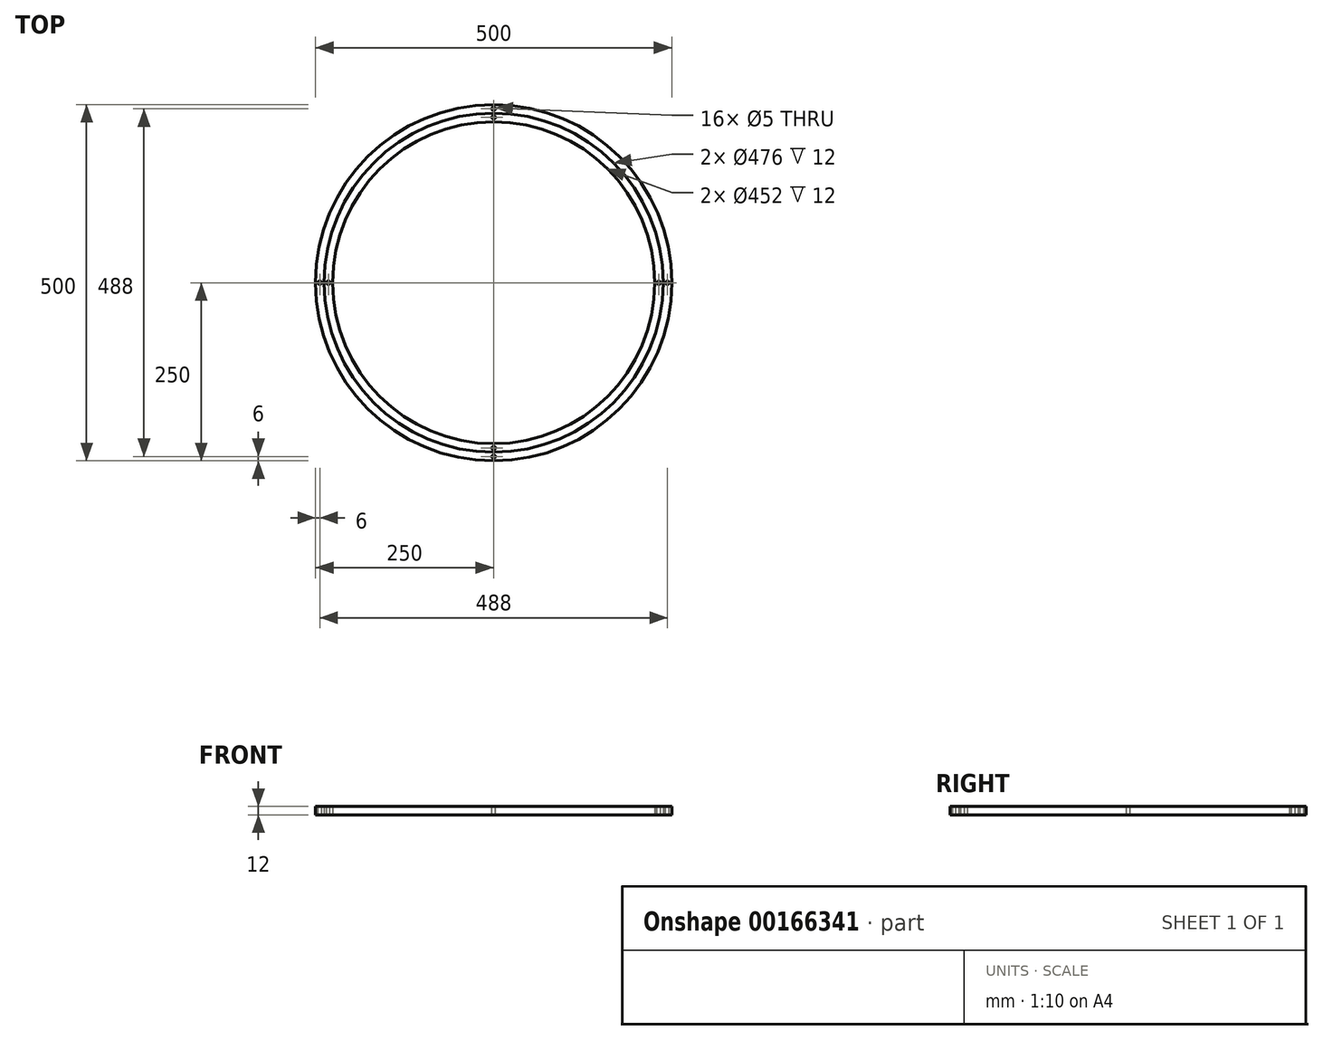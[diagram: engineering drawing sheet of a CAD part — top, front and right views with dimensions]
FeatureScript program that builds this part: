
annotation { "Feature Type Name" : "Feature", "Feature Type Description" : "" }
export const myFeature = defineFeature(function(context is Context, id is Id, definition is map)
    precondition{}
    {
        {
            var Q0;
            Q0=qCreatedBy(makeId("Top.planeOp"),FACE);
            var sketch = newSketch(context, id + "F0", { "sketchPlane" : qUnion([Q0])});
            skCircle(sketch, "E0", {"center": v(0, 0) * mm, "radius": 250 * mm});
            skCircle(sketch, "E1", {"center": v(0, 0) * mm, "radius": 238 * mm});
            skSolve(sketch);
        }
        {
            var Q0;
            Q0=makeQuery(id+"F0.imprint","IMPRINT",FACE,{"disambiguationData":[TD([[makeQuery(id+"F0.imprint","IMPRINT",EDGE,{"derivedFrom":sQuery(id+"F0.wireOp",EDGE,"E0")}),1.0]])]});
            extrude(context, id + "F1", {"entities" : qUnion([Q0]), "depth" : 12 * mm});
        }
        {
            var Q0;
            Q0=qCreatedBy(makeId("Top.planeOp"),FACE);
            var sketch = newSketch(context, id + "F2", { "sketchPlane" : qUnion([Q0])});
            skCircle(sketch, "E2", {"center": v(0, 0) * mm, "radius": 238 * mm});
            skCircle(sketch, "E3", {"center": v(0, 0) * mm, "radius": 226 * mm});
            skSolve(sketch);
        }
        {
            var Q0;
            Q0 = qSketchRegion(id + "F2", true);
            extrude(context, id + "F3", {"entities" : qUnion([Q0]), "depth" : 12 * mm});
        }
        {
            var Q0;
            Q0=makeQuery(id+"F3.opExtrude","CAP_FACE",FACE,{"disambiguationData":[OSD([sQuery(id+"F2.wireOp",EDGE,"E2"),sQuery(id+"F2.wireOp",EDGE,"E3")])],"isStart":false});
            var sketch = newSketch(context, id + "F4", { "sketchPlane" : qUnion([Q0])});
            skLineSegment(sketch, "E4", {"start": v(0, 0) * mm, "end": v(0, 232) * mm});
            skCircle(sketch, "E5", {"center": v(0, 232) * mm, "radius": 2.5 * mm});
            skCircle(sketch, "E6.1.0", {"center": v(-232, 0) * mm, "radius": 2.5 * mm});
            skCircle(sketch, "E6.2.0", {"center": v(0, -232) * mm, "radius": 2.5 * mm});
            skCircle(sketch, "E6.3.0", {"center": v(232, 0) * mm, "radius": 2.5 * mm});
            skPoint(sketch, "E6.center", {"position": v(0, 0) * mm});
            skSolve(sketch);
        }
        {
            var Q0;
            Q0 = qSketchRegion(id + "F4", true);
            extrude(context, id + "F5", {"entities" : qUnion([Q0]), "operationType" : NewBodyOperationType.REMOVE, "oppositeDirection" : true, "depth" : 12 * mm});
        }
        {
            var Q0;
            Q0=makeQuery(id+"F1.opExtrude","CAP_FACE",FACE,{"disambiguationData":[OSD([sQuery(id+"F0.wireOp",EDGE,"E0"),sQuery(id+"F0.wireOp",EDGE,"E1")])],"isStart":false});
            var sketch = newSketch(context, id + "F6", { "sketchPlane" : qUnion([Q0])});
            skLineSegment(sketch, "E7", {"start": v(0, 0) * mm, "end": v(0, 244) * mm});
            skCircle(sketch, "E8", {"center": v(0, 244) * mm, "radius": 2.5 * mm});
            skCircle(sketch, "E9.1.0", {"center": v(-244, 0) * mm, "radius": 2.5 * mm});
            skCircle(sketch, "E9.2.0", {"center": v(0, -244) * mm, "radius": 2.5 * mm});
            skCircle(sketch, "E9.3.0", {"center": v(244, 0) * mm, "radius": 2.5 * mm});
            skPoint(sketch, "E9.center", {"position": v(0, 0) * mm});
            skSolve(sketch);
        }
        {
            var Q0;
            Q0 = qSketchRegion(id + "F6", true);
            extrude(context, id + "F7", {"entities" : qUnion([Q0]), "operationType" : NewBodyOperationType.REMOVE, "oppositeDirection" : true, "depth" : 12 * mm});
        }
    });
